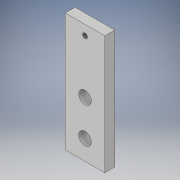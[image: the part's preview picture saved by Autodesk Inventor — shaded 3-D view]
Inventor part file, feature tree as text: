
AUTODESK INVENTOR PART (.ipt)
format: ipt  version: 2017 (Build 210142000, 142)  size: 112,640 bytes
history: native  units: in
note: dims shown in document units (in); Inventor stores cm internally (conversion verified against a paired STEP export)
features: sketch x3, hole x2, extrude x1
ambient origin geometry x8: Origin, YZ Plane, XZ Plane, XY Plane, X Axis, Y Axis, Z Axis, Center Point
bodies: Solid1 (feature_tree)
feature tree (6):
  extrude  "Extrusion1"  Depth=1.5in
  sketch  "Sketch2"  dims[d2=0.125in d3=0.0in]
  hole  "Hole1"  [1 undecoded]
  hole  "Hole3"  [1 undecoded]
  sketch  "Sketch1"  dims[d0=0.5in d1=1.5in]
  sketch  "Sketch3"  dims[d6=0.062in d7=0.157in d8=0.375in d9=0.25in d10=0.5635in d11=0.248in d12=0.8108in d23=0.125in d24=0.25in d25=0.25in d26=0.45in d27=0.16in d28=0.75in d29=0.375in d30=0.25in d31=0.5635in d32=1.0in d33=0.8108in]
note: 2 required parameter values undecoded (feature->parameter linkage not recoverable at this tier; creation-order binding heuristic only, values carry confidence <= 0.55)
